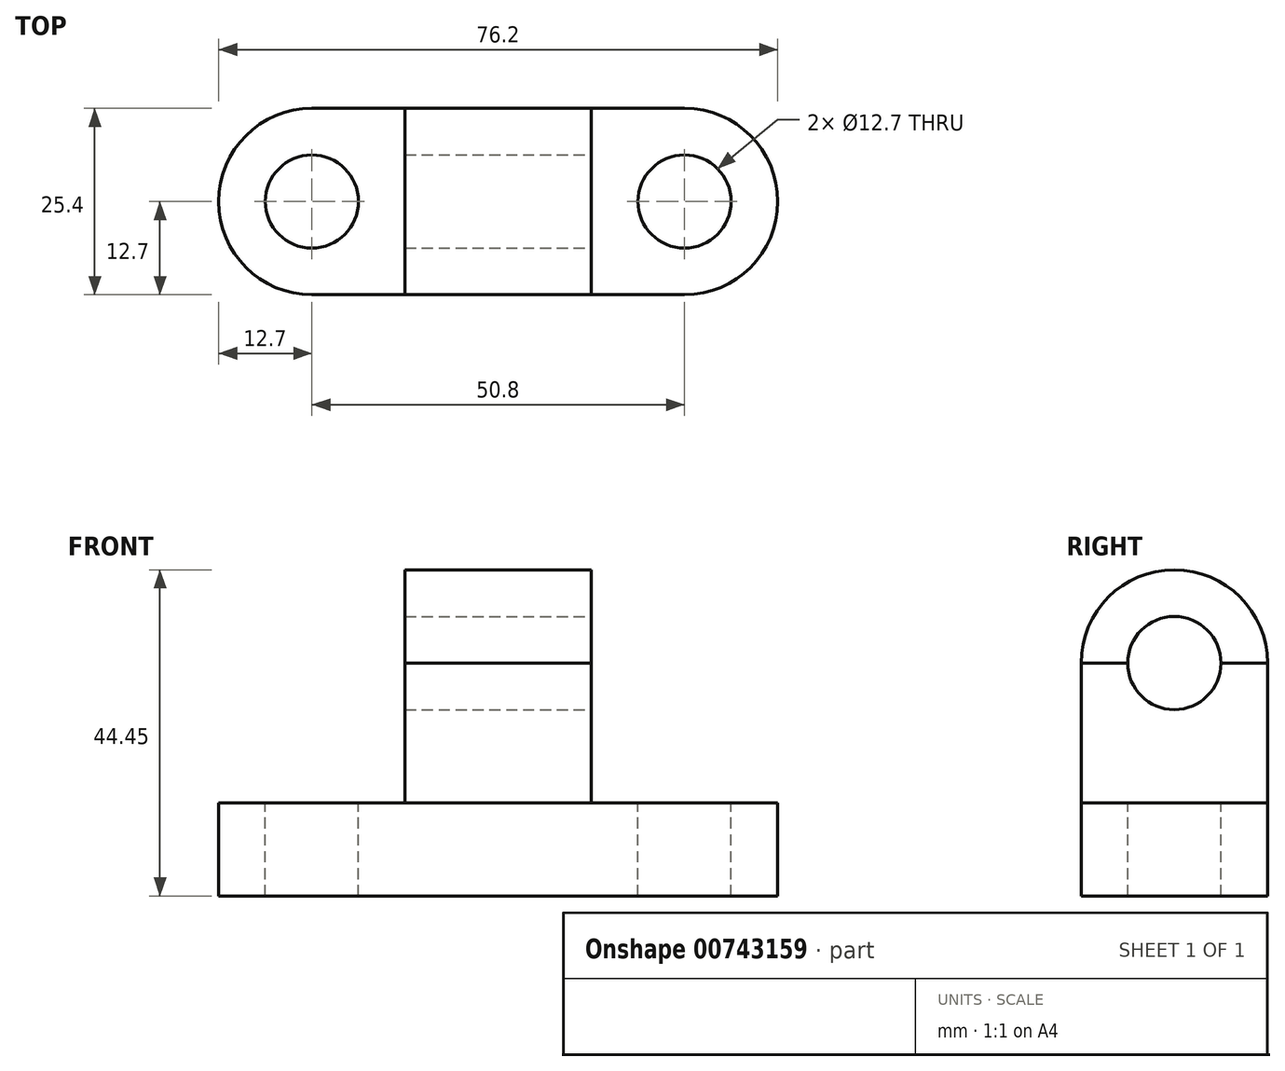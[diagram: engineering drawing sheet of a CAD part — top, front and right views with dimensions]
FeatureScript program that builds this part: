
annotation { "Feature Type Name" : "Feature", "Feature Type Description" : "" }
export const myFeature = defineFeature(function(context is Context, id is Id, definition is map)
    precondition{}
    {
        {
            var Q0;
            Q0=qCreatedBy(makeId("Top.planeOp"),FACE);
            var sketch = newSketch(context, id + "F0", { "sketchPlane" : qUnion([Q0])});
            skLineSegment(sketch, "E0", {"start": v(0, 0) * mm, "end": v(50.8, 0) * mm});
            skLineSegment(sketch, "E1", {"start": v(50.8, 0) * mm, "end": v(50.8, 25.4) * mm});
            skLineSegment(sketch, "E2", {"start": v(50.8, 25.4) * mm, "end": v(0, 25.4) * mm});
            skLineSegment(sketch, "E3", {"start": v(0, 25.4) * mm, "end": v(0, 0) * mm});
            skArc(sketch, "E4", {"start": v(0, 25.4) * mm, "mid": v(-12.7, 12.7) * mm, "end": v(0, 0) * mm});
            skArc(sketch, "E5", {"start": v(50.8, 0) * mm, "mid": v(63.5, 12.7) * mm, "end": v(50.8, 25.4) * mm});
            skSolve(sketch);
        }
        {
            var Q0;
            Q0=makeQuery(id+"F0.imprint","IMPRINT",FACE,{"disambiguationData":[TD([[makeQuery(id+"F0.imprint","IMPRINT",EDGE,{"derivedFrom":sQuery(id+"F0.wireOp",EDGE,"E3")}),-1.0]])]});
            var Q1;
            Q1=makeQuery(id+"F0.imprint","IMPRINT",FACE,{"disambiguationData":[TD([[makeQuery(id+"F0.imprint","IMPRINT",EDGE,{"derivedFrom":sQuery(id+"F0.wireOp",EDGE,"E0")}),1.0]])]});
            var Q2;
            Q2=makeQuery(id+"F0.imprint","IMPRINT",FACE,{"disambiguationData":[TD([[makeQuery(id+"F0.imprint","IMPRINT",EDGE,{"derivedFrom":sQuery(id+"F0.wireOp",EDGE,"E1")}),-1.0]])]});
            extrude(context, id + "F1", {"entities" : qUnion([Q0, Q1, Q2]), "depth" : 12.7 * mm, "offsetDistance" : 25.4 * mm});
        }
        {
            var Q0;
            Q0=makeQuery(id+"F1.opExtrude","CAP_FACE",FACE,{"disambiguationData":[OSD([sQuery(id+"F0.wireOp",EDGE,"E0"),sQuery(id+"F0.wireOp",EDGE,"E2"),sQuery(id+"F0.wireOp",EDGE,"E4"),sQuery(id+"F0.wireOp",EDGE,"E5")])],"isStart":false});
            var sketch = newSketch(context, id + "F2", { "sketchPlane" : qUnion([Q0])});
            skCircle(sketch, "E6", {"center": v(0, 12.7) * mm, "radius": 6.35 * mm});
            skCircle(sketch, "E7", {"center": v(50.8, 12.7) * mm, "radius": 6.35 * mm});
            skSolve(sketch);
        }
        {
            var Q0;
            Q0=makeQuery(id+"F2.imprint","IMPRINT",FACE,{"disambiguationData":[TD([[makeQuery(id+"F2.imprint","IMPRINT",EDGE,{"derivedFrom":sQuery(id+"F2.wireOp",EDGE,"E6")}),1.0]])]});
            var Q1;
            Q1=makeQuery(id+"F2.imprint","IMPRINT",FACE,{"disambiguationData":[TD([[makeQuery(id+"F2.imprint","IMPRINT",EDGE,{"derivedFrom":sQuery(id+"F2.wireOp",EDGE,"E7")}),1.0]])]});
            extrude(context, id + "F3", {"entities" : qUnion([Q0, Q1]), "operationType" : NewBodyOperationType.REMOVE, "oppositeDirection" : true, "depth" : 25.4 * mm, "offsetDistance" : 25.4 * mm});
        }
        {
            var Q0;
            Q0=makeQuery(id+"F1.opExtrude","SWEPT_FACE",FACE,{"disambiguationData":[OSD([sQuery(id+"F0.wireOp",EDGE,"E0")])]});
            var sketch = newSketch(context, id + "F4", { "sketchPlane" : qUnion([Q0])});
            skLineSegment(sketch, "E8.bottom", {"start": v(12.7, 12.7) * mm, "end": v(38.1, 12.7) * mm});
            skLineSegment(sketch, "E8.top", {"start": v(12.7, 31.75) * mm, "end": v(38.1, 31.75) * mm});
            skLineSegment(sketch, "E8.left", {"start": v(12.7, 12.7) * mm, "end": v(12.7, 31.75) * mm});
            skLineSegment(sketch, "E8.right", {"start": v(38.1, 12.7) * mm, "end": v(38.1, 31.75) * mm});
            skSolve(sketch);
        }
        {
            var Q0;
            Q0=makeQuery(id+"F4.imprint","IMPRINT",FACE,{"disambiguationData":[TD([[makeQuery(id+"F4.imprint","IMPRINT",EDGE,{"derivedFrom":sQuery(id+"F4.wireOp",EDGE,"E8.bottom")}),1.0]])]});
            extrude(context, id + "F5", {"entities" : qUnion([Q0]), "oppositeDirection" : true, "depth" : 25.4 * mm, "offsetDistance" : 25.4 * mm});
        }
        {
            var Q0;
            Q0=makeQuery(id+"F5.opExtrude","SWEPT_FACE",FACE,{"disambiguationData":[OSD([sQuery(id+"F4.wireOp",EDGE,"E8.right")])]});
            var sketch = newSketch(context, id + "F6", { "sketchPlane" : qUnion([Q0])});
            skArc(sketch, "E9", {"start": v(25.4, 31.75) * mm, "mid": v(12.7, 44.45) * mm, "end": v(0, 31.75) * mm});
            skSolve(sketch);
        }
        {
            var Q0;
            Q0=makeQuery(id+"F6.imprint","IMPRINT",FACE,{"disambiguationData":[TD([[makeQuery(id+"F6.imprint","IMPRINT",EDGE,{"derivedFrom":sQuery(id+"F6.wireOp",EDGE,"E9")}),1.0]])]});
            extrude(context, id + "F7", {"entities" : qUnion([Q0]), "oppositeDirection" : true, "depth" : 25.4 * mm, "offsetDistance" : 25.4 * mm});
        }
        {
            var Q0;
            Q0=makeQuery(id+"F5.opExtrude","SWEPT_FACE",FACE,{"disambiguationData":[OSD([sQuery(id+"F4.wireOp",EDGE,"E8.right")])]});
            var sketch = newSketch(context, id + "F8", { "sketchPlane" : qUnion([Q0])});
            skCircle(sketch, "E10", {"center": v(12.7, 31.75) * mm, "radius": 6.35 * mm});
            skSolve(sketch);
        }
        {
            var Q0;
            {var subQ0=sQuery(id+"F8.wireOp",EDGE,"E10");var subQ1=makeQuery(id+"F5.opExtrude","SWEPT_EDGE",EDGE,{"disambiguationData":[OSD([sQuery(id+"F4.wireOp",EDGE,"E8.top"),sQuery(id+"F4.wireOp",EDGE,"E8.right")])]});var subQ2=makeQuery(id+"F8.imprint","INTERSECT",VERTEX,{"disambiguationData":[OD(0.0)],"derivedFrom":[subQ1,subQ0]});Q0=makeQuery(id+"F8.imprint","IMPRINT",FACE,{"disambiguationData":[TD([[makeQuery(id+"F8.imprint","IMPRINT",EDGE,{"disambiguationData":[TD([[subQ2,1.0]])],"derivedFrom":subQ0}),1.0]])]});}
            var Q1;
            {var subQ0=sQuery(id+"F8.wireOp",EDGE,"E10");var subQ1=makeQuery(id+"F5.opExtrude","SWEPT_EDGE",EDGE,{"disambiguationData":[OSD([sQuery(id+"F4.wireOp",EDGE,"E8.top"),sQuery(id+"F4.wireOp",EDGE,"E8.right")])]});var subQ2=makeQuery(id+"F8.imprint","INTERSECT",VERTEX,{"disambiguationData":[OD(0.0)],"derivedFrom":[subQ1,subQ0]});Q1=makeQuery(id+"F8.imprint","IMPRINT",FACE,{"disambiguationData":[TD([[makeQuery(id+"F8.imprint","IMPRINT",EDGE,{"disambiguationData":[TD([[subQ2,-1.0]])],"derivedFrom":subQ0}),1.0]])]});}
            extrude(context, id + "F9", {"entities" : qUnion([Q0, Q1]), "operationType" : NewBodyOperationType.REMOVE, "oppositeDirection" : true, "depth" : 25.4 * mm, "offsetDistance" : 25.4 * mm});
        }
        {
            var Q0;
            Q0=makeQuery(id+"F5.opExtrude","SWEPT_FACE",FACE,{"disambiguationData":[OSD([sQuery(id+"F4.wireOp",EDGE,"E8.right")])]});
            var sketch = newSketch(context, id + "F10", { "sketchPlane" : qUnion([Q0])});
            skCircle(sketch, "E11", {"center": v(12.7, 31.75) * mm, "radius": 6.35 * mm});
            skSolve(sketch);
        }
        {
            var Q0;
            {var subQ0=sQuery(id+"F10.wireOp",EDGE,"E11");var subQ1=makeQuery(id+"F5.opExtrude","SWEPT_EDGE",EDGE,{"disambiguationData":[OSD([sQuery(id+"F4.wireOp",EDGE,"E8.top"),sQuery(id+"F4.wireOp",EDGE,"E8.right")])]});var subQ2=makeQuery(id+"F10.imprint","INTERSECT",VERTEX,{"disambiguationData":[OD(0.0)],"derivedFrom":[subQ1,subQ0]});Q0=makeQuery(id+"F10.imprint","IMPRINT",FACE,{"disambiguationData":[TD([[makeQuery(id+"F10.imprint","IMPRINT",EDGE,{"disambiguationData":[TD([[subQ2,-1.0]])],"derivedFrom":subQ0}),1.0]])]});}
            extrude(context, id + "F11", {"entities" : qUnion([Q0]), "operationType" : NewBodyOperationType.REMOVE, "oppositeDirection" : true, "depth" : 25.4 * mm, "offsetDistance" : 25.4 * mm});
        }
    });
